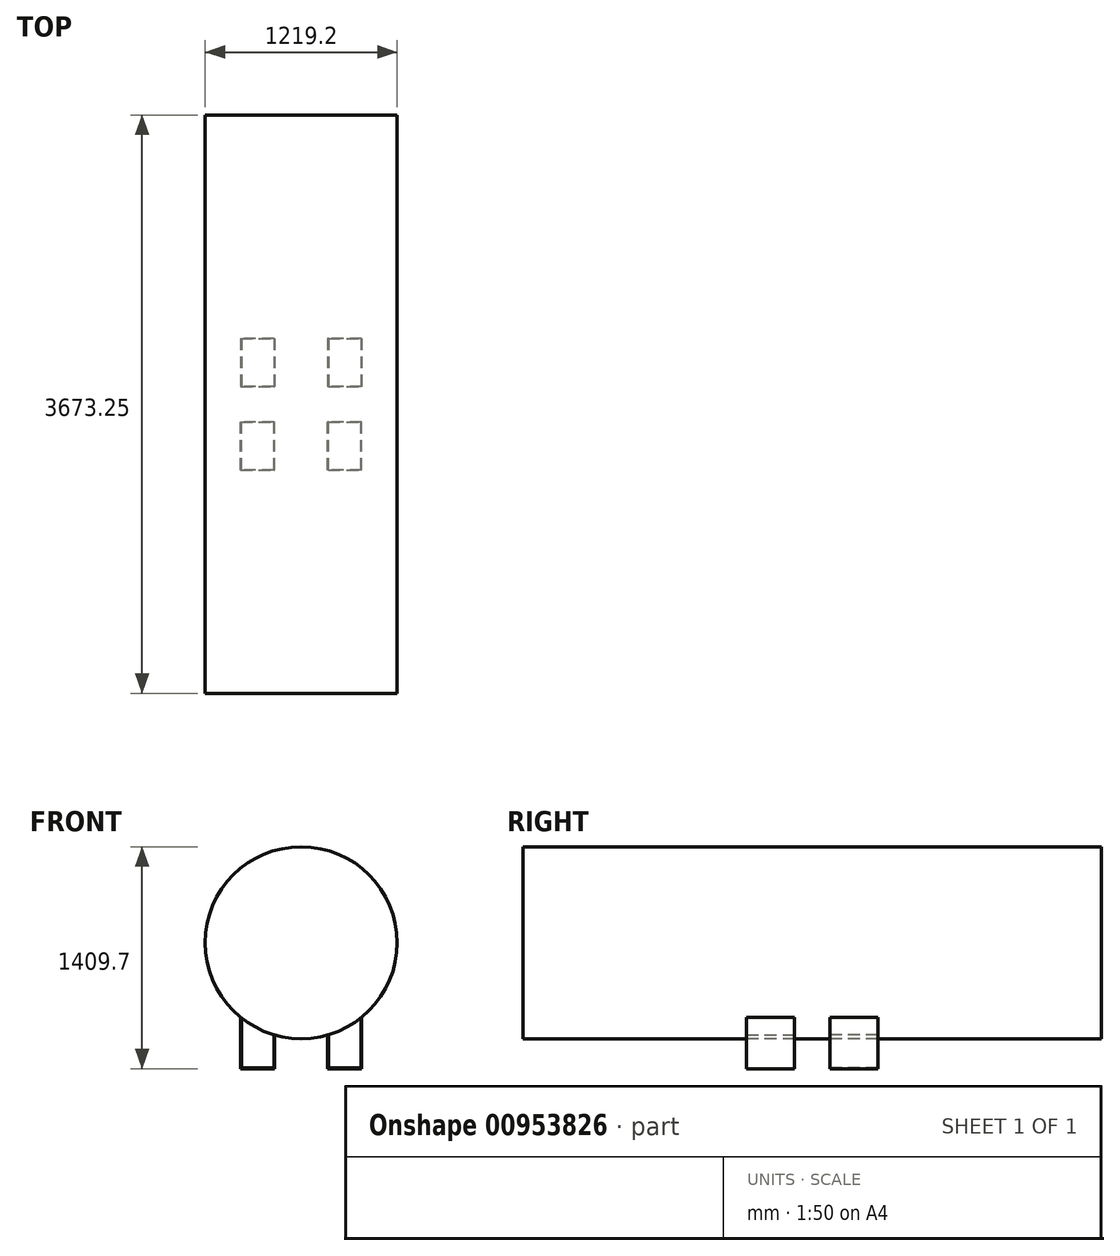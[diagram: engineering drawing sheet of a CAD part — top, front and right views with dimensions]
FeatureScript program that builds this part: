
annotation { "Feature Type Name" : "Feature", "Feature Type Description" : "" }
export const myFeature = defineFeature(function(context is Context, id is Id, definition is map)
    precondition{}
    {
        {
            var Q0;
            Q0=qCreatedBy(makeId("Front.planeOp"),FACE);
            var sketch = newSketch(context, id + "F0", { "sketchPlane" : qUnion([Q0])});
            skCircle(sketch, "E0", {"center": v(0, 0) * mm, "radius": 609.6 * mm});
            skSolve(sketch);
        }
        {
            var Q0;
            Q0=makeQuery(id+"F0.imprint","IMPRINT",FACE,{"disambiguationData":[TD([[makeQuery(id+"F0.imprint","IMPRINT",EDGE,{"derivedFrom":sQuery(id+"F0.wireOp",EDGE,"E0")}),1.0]])]});
            extrude(context, id + "F1", {"entities" : qUnion([Q0]), "oppositeDirection" : true, "depth" : 1873.25 * mm, "offsetDistance" : 25.4 * mm});
        }
        {
            var Q0;
            Q0=makeQuery(id+"F1.opExtrude","CAP_FACE",FACE,{"disambiguationData":[OSD([sQuery(id+"F0.wireOp",EDGE,"E0")])],"isStart":true});
            cPlane(context, id + "F2", {"entities" : qUnion([Q0]), "cplaneType" : CPlaneType.OFFSET, "offset" : 149.22 * mm, "oppositeDirection" : true, "width" : 152.4 * mm, "height" : 152.4 * mm});
        }
        {
            var Q0;
            Q0=qCreatedBy(id+"F2.planeOp",FACE);
            var sketch = newSketch(context, id + "F3", { "sketchPlane" : qUnion([Q0])});
            skLineSegment(sketch, "E1.bottom", {"start": v(-384.17, -800.1) * mm, "end": v(-168.27, -800.1) * mm});
            skLineSegment(sketch, "E1.left", {"start": v(-384.17, -800.1) * mm, "end": v(-384.17, -473.3) * mm});
            skLineSegment(sketch, "E1.right", {"start": v(-168.27, -800.1) * mm, "end": v(-168.27, -585.91) * mm});
            skLineSegment(sketch, "E2.bottom", {"start": v(-173.04, -795.34) * mm, "end": v(-379.41, -795.34) * mm});
            skLineSegment(sketch, "E2.left", {"start": v(-173.04, -795.34) * mm, "end": v(-173.04, -584.53) * mm});
            skLineSegment(sketch, "E2.right", {"start": v(-379.41, -795.34) * mm, "end": v(-379.41, -477.14) * mm});
            skArc(sketch, "E3", {"start": v(-384.17, -473.3) * mm, "mid": v(-281.9, -540.5) * mm, "end": v(-168.27, -585.91) * mm});
            skSolve(sketch);
        }
        {
            var Q0;
            Q0=makeQuery(id+"F3.imprint","IMPRINT",FACE,{"disambiguationData":[TD([[makeQuery(id+"F3.imprint","IMPRINT",EDGE,{"derivedFrom":sQuery(id+"F3.wireOp",EDGE,"E1.bottom")}),1.0]])]});
            extrude(context, id + "F4", {"entities" : qUnion([Q0]), "operationType" : NewBodyOperationType.ADD, "oppositeDirection" : true, "depth" : 304.8 * mm, "offsetDistance" : 25.4 * mm});
        }
        {
            var Q0;
            Q0=makeQuery(id+"F1.opExtrude","SWEPT_BODY",BODY,{"disambiguationData":[OSD([sQuery(id+"F0.wireOp",EDGE,"E0")])]});
            var Q1;
            Q1=qCreatedBy(makeId("Right.planeOp"),FACE);
            mirror(context, id + "F5", {"operationType" : NewBodyOperationType.ADD, "entities" : qUnion([Q0]), "mirrorPlane" : qUnion([Q1])});
        }
        {
            var Q0;
            Q0=makeQuery(id+"F1.opExtrude","CAP_FACE",FACE,{"disambiguationData":[OSD([sQuery(id+"F0.wireOp",EDGE,"E0")])],"isStart":true});
            cPlane(context, id + "F6", {"entities" : qUnion([Q0]), "cplaneType" : CPlaneType.OFFSET, "offset" : (12 + 5 + 7 / 8 + (37.5) / 2) * mm, "oppositeDirection" : true, "width" : 152.4 * mm, "height" : 152.4 * mm});
        }
        {
            var Q0;
            Q0=makeQuery(id+"F1.opExtrude","SWEPT_BODY",BODY,{"disambiguationData":[OSD([sQuery(id+"F0.wireOp",EDGE,"E0")])]});
            var Q1;
            Q1=qCreatedBy(id+"F6.planeOp",FACE);
            mirror(context, id + "F7", {"operationType" : NewBodyOperationType.ADD, "entities" : qUnion([Q0]), "mirrorPlane" : qUnion([Q1])});
        }
    });
